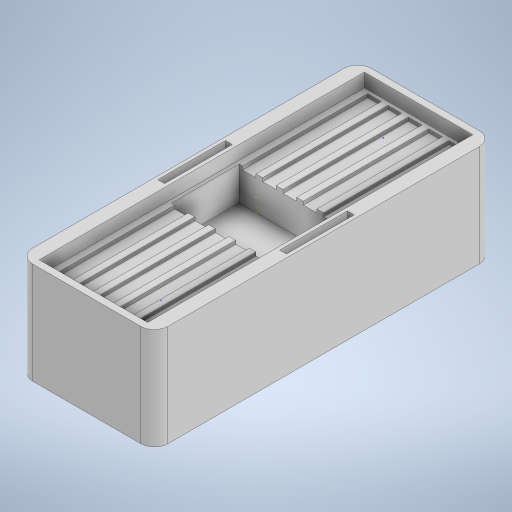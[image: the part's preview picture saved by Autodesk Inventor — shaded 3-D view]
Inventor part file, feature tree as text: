
AUTODESK INVENTOR PART (.ipt)
format: ipt  version: 2023.1 (Build 271208000, 208)  size: 896,000 bytes
history: native  units: mm
features: sketch x9, extrude x5, other x2, fillet x1
ambient origin geometry x8: Origin, YZ Plane, XZ Plane, XY Plane, X Axis, Y Axis, Z Axis, Center Point
bodies: Volumenkörper1 (feature_tree)
feature tree (17):
  extrude  "Extrusion1"  Depth=20.0mm
  extrude  "Extrusion2"  Depth=1.0mm
  sketch  "Skizze4"  dims[d5=1.0mm d6=2.0mm]
  sketch  "Skizze5"  dims[d7=2.0mm d8=2.0mm d9=0.0mm]
  extrude  "Extrusion3"  Depth=1.0mm
  sketch  "Skizze6"  dims[d10=2.0mm d11=0.5mm d12=0.5mm]
  other  "3D-Skizze1"
  sketch  "Skizze8"  dims[d13=0.5mm d14=0.0mm]
  extrude  "Extrusion5"  Depth=2.0mm TaperAngle=0.0deg
  extrude  "Extrusion6"  Depth=0.5mm
  fillet  "Rundung1"  Radius=0.5mm
  other  "Prägen1"
  sketch  "Skizze1"  dims[d0=50.0mm d1=20.0mm]
  sketch  "Skizze3"  dims[d2=15.0mm d3=0.0mm d4=1.0mm]
  sketch  "Skizze9"  dims[d20=10.0mm]
  sketch  "Skizze10"  dims[d21=25.0mm]
  sketch  "Skizze11"  dims[d23=10.0mm d24=0.5mm d25=1.0mm d26=0.0mm d29=1.0mm d30=0.5mm d31=5.0mm d32=0.0mm d33=2.0mm d34=2.0mm d35=2.0mm d36=2.0mm d37=1.0mm d38=1.0mm d39=1.0mm d40=1.0mm d41=1.0mm d42=1.0mm d43=0.5mm d44=0.5mm d45=10.0mm d46=19.0mm d47=5.0mm d48=0.0mm d49=2.0mm d50=47.0mm d51=0.5mm d52=0.5mm d53=0.5mm d54=0.5mm d55=47.0mm d56=6.0mm d57=7.5mm d58=35.0mm d59=8.0mm d60=1.0mm d61=0.0mm d18=0.5mm d19=0.872665mm]
